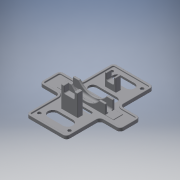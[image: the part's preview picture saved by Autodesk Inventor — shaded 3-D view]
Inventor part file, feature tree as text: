
AUTODESK INVENTOR PART (.ipt)
format: ipt  version: 2017 (Build 210142000, 142)  size: 665,088 bytes
history: native  units: in
note: dims shown in document units (in); Inventor stores cm internally (conversion verified against a paired STEP export)
features: extrude x8, sketch x8, fillet x4, plane x2, projected_geometry x2
ambient origin geometry x8: Origin, YZ Plane, XZ Plane, XY Plane, X Axis, Y Axis, Z Axis, Center Point
bodies: Solid1 (feature_tree)
feature tree (24):
  extrude  "Base"  Depth=5.1181in
  extrude  "rear_wing"  TaperAngle=90.0deg  [1 undecoded]
  extrude  "cut"  Depth=0.1181in
  plane  "Work Plane1"
  extrude  "wheel_holder"  Depth=0.5512in
  plane  "Work Plane2"
  extrude  "Upper_wing"  Depth=0.5512in
  extrude  "Extrusion8"  Depth=0.1181in
  fillet  "Fillet 1mm"  Radius=2.3622in
  fillet  "Fillet 5mm"  Radius=1.9685in
  extrude  "Border"  Depth=0.9055in
  fillet  "Fillet3"  Radius=0.1969in
  extrude  "Slot"  TaperAngle=90.0deg  [1 undecoded]
  fillet  "Fillet4"  Radius=0.5906in
  sketch  "Sketch1"  dims[d0=4.7244in d1=5.1181in]
  sketch  "Sketch2"  dims[d2=0.1181in d3=0.0in d4=90.0deg]
  sketch  "Sketch3"  dims[d5=0.1181in d6=0.1181in]
  sketch  "Sketch4"  dims[d7=0.315in d9=0.5512in]
  sketch  "Sketch5"  dims[d10=0.5512in d11=0.1575in]
  projected_geometry  "Projected Loop1"
  sketch  "Sketch6"  dims[d12=0.1181in d13=0.0394in d14=2.3622in d15=0.0in d16=1.9685in]
  projected_geometry  "Projected Loop2"
  sketch  "Sketch7"  dims[d17=1.1811in d18=0.0in d19=0.9055in d21=0.1969in]
  sketch  "Sketch8"  dims[d22=0.1969in d24=90.0deg d25=0.5906in d26=0.3937in d28=0.9843in d29=0.4921in d30=0.0394in d31=0.0591in d32=0.315in d33=0.0in d34=-1.1811in d35=0.4173in d36=0.2087in d37=0.1181in d38=0.1181in d39=0.3937in d40=0.3937in d42=0.0787in d43=0.0394in d44=0.315in d45=0.0in d46=0.0394in d47=1.1811in d48=1.9685in d49=0.1575in d50=0.9843in d51=0.4724in d52=0.1969in d53=0.1181in d54=0.0787in d55=0.0in d56=0.0276in d57=0.1969in d58=0.1969in d59=2.1654in d60=2.0866in d61=0.8859in d62=0.8859in d63=0.3937in d64=0.5118in d65=0.5906in d66=0.4724in d67=0.4331in d68=0.5906in d69=0.0787in d70=0.0in d71=0.5906in d72=0.1969in d73=0.0in d74=0.4724in d75=0.0394in d76=0.0in d77=0.0197in]
note: 2 required parameter values undecoded (feature->parameter linkage not recoverable at this tier; creation-order binding heuristic only, values carry confidence <= 0.55)
